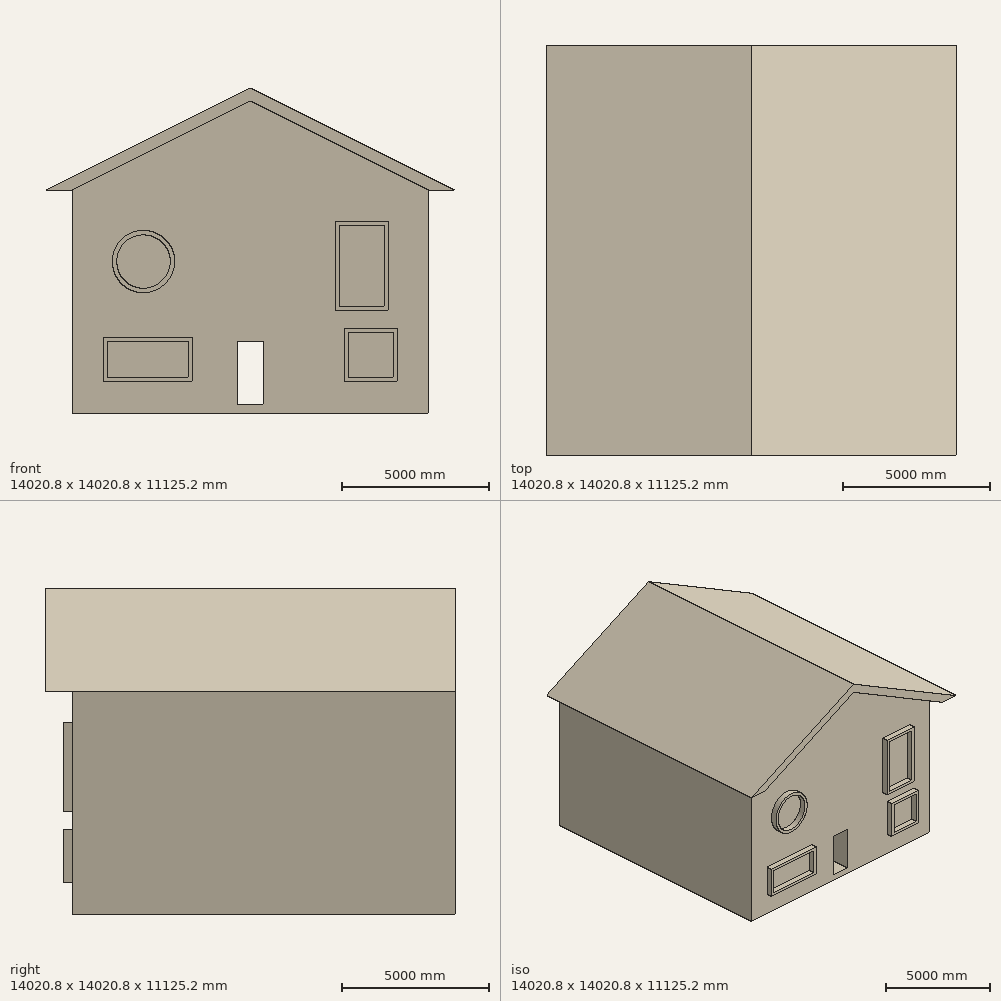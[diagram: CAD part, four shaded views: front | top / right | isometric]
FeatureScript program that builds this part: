
annotation { "Feature Type Name" : "Feature", "Feature Type Description" : "" }
export const myFeature = defineFeature(function(context is Context, id is Id, definition is map)
    precondition{}
    {
        {
            var Q0;
            Q0=qCreatedBy(makeId("Front.planeOp"),FACE);
            var sketch = newSketch(context, id + "F0", { "sketchPlane" : qUnion([Q0])});
            skLineSegment(sketch, "E0", {"start": v(0, 0) * mm, "end": v(-6096, 0) * mm});
            skLineSegment(sketch, "E1", {"start": v(0, 0) * mm, "end": v(6096, 0) * mm});
            skLineSegment(sketch, "E2", {"start": v(0, 0) * mm, "end": v(0, 3048) * mm, "construction": true});
            skLineSegment(sketch, "E3", {"start": v(-6096, 0) * mm, "end": v(0, 3048) * mm});
            skLineSegment(sketch, "E4", {"start": v(0, 3048) * mm, "end": v(6096, 0) * mm});
            skLineSegment(sketch, "E5", {"start": v(-6096, 0) * mm, "end": v(-7010.4, 0) * mm});
            skLineSegment(sketch, "E6", {"start": v(6096, 0) * mm, "end": v(7010.4, 0) * mm});
            skLineSegment(sketch, "E7", {"start": v(0, 3048) * mm, "end": v(0, 3505.2) * mm});
            skLineSegment(sketch, "E8", {"start": v(-7010.4, 0) * mm, "end": v(0, 3505.2) * mm});
            skLineSegment(sketch, "E9", {"start": v(0, 3505.2) * mm, "end": v(7010.4, 0) * mm});
            skLineSegment(sketch, "E10", {"start": v(-6096, 0) * mm, "end": v(-6096, -7315.2) * mm});
            skLineSegment(sketch, "E11", {"start": v(-6096, -7315.2) * mm, "end": v(6096, -7315.2) * mm});
            skLineSegment(sketch, "E12", {"start": v(6096, -7315.2) * mm, "end": v(6096, 0) * mm});
            skLineSegment(sketch, "E13", {"start": v(-6096, -7315.2) * mm, "end": v(-6096, -6423.42) * mm});
            skLineSegment(sketch, "E14", {"start": v(-6096, -7315.2) * mm, "end": v(-6096, -7620) * mm});
            skLineSegment(sketch, "E15", {"start": v(-6096, -7620) * mm, "end": v(6096, -7620) * mm});
            skLineSegment(sketch, "E16", {"start": v(6096, -7315.2) * mm, "end": v(6096, -7620) * mm});
            skLineSegment(sketch, "E17", {"start": v(0, -7315.2) * mm, "end": v(-457.2, -7315.2) * mm});
            skLineSegment(sketch, "E18", {"start": v(-457.2, -7315.2) * mm, "end": v(-457.2, -5181.6) * mm});
            skLineSegment(sketch, "E19", {"start": v(-457.2, -5181.6) * mm, "end": v(457.2, -5181.6) * mm});
            skLineSegment(sketch, "E20", {"start": v(457.2, -5181.6) * mm, "end": v(457.2, -7315.2) * mm});
            skLineSegment(sketch, "E21", {"start": v(0, -7315.2) * mm, "end": v(457.2, -7315.2) * mm});
            skLineSegment(sketch, "E22.bottom", {"start": v(-2133.6, -5181.6) * mm, "end": v(-4876.8, -5181.6) * mm});
            skLineSegment(sketch, "E22.top", {"start": v(-2133.6, -6400.8) * mm, "end": v(-4876.8, -6400.8) * mm});
            skLineSegment(sketch, "E22.left", {"start": v(-2133.6, -5181.6) * mm, "end": v(-2133.6, -6400.8) * mm});
            skLineSegment(sketch, "E22.right", {"start": v(-4876.8, -5181.6) * mm, "end": v(-4876.8, -6400.8) * mm});
            skLineSegment(sketch, "E23.0", {"start": v(-1981.2, -5029.2) * mm, "end": v(-1981.2, -6553.2) * mm});
            skLineSegment(sketch, "E23.1", {"start": v(-1981.2, -5029.2) * mm, "end": v(-5029.2, -5029.2) * mm});
            skLineSegment(sketch, "E23.2", {"start": v(-5029.2, -5029.2) * mm, "end": v(-5029.2, -6553.2) * mm});
            skLineSegment(sketch, "E23.3", {"start": v(-1981.2, -6553.2) * mm, "end": v(-5029.2, -6553.2) * mm});
            skLineSegment(sketch, "E24.bottom", {"start": v(3352.8, -4876.8) * mm, "end": v(4876.8, -4876.8) * mm});
            skLineSegment(sketch, "E24.top", {"start": v(3352.8, -6400.8) * mm, "end": v(4876.8, -6400.8) * mm});
            skLineSegment(sketch, "E24.left", {"start": v(3352.8, -4876.8) * mm, "end": v(3352.8, -6400.8) * mm});
            skLineSegment(sketch, "E24.right", {"start": v(4876.8, -4876.8) * mm, "end": v(4876.8, -6400.8) * mm});
            skLineSegment(sketch, "E25.0", {"start": v(5029.2, -4724.4) * mm, "end": v(5029.2, -6553.2) * mm});
            skLineSegment(sketch, "E25.1", {"start": v(3200.4, -4724.4) * mm, "end": v(5029.2, -4724.4) * mm});
            skLineSegment(sketch, "E25.2", {"start": v(3200.4, -4724.4) * mm, "end": v(3200.4, -6553.2) * mm});
            skLineSegment(sketch, "E25.3", {"start": v(3200.4, -6553.2) * mm, "end": v(5029.2, -6553.2) * mm});
            skCircle(sketch, "E26", {"center": v(-3657.6, -2438.4) * mm, "radius": 914.4 * mm});
            skCircle(sketch, "E27.0", {"center": v(-3657.6, -2438.4) * mm, "radius": 1066.8 * mm});
            skLineSegment(sketch, "E28.bottom", {"start": v(3048, -1219.2) * mm, "end": v(4572, -1219.2) * mm});
            skLineSegment(sketch, "E28.top", {"start": v(3048, -3962.4) * mm, "end": v(4572, -3962.4) * mm});
            skLineSegment(sketch, "E28.left", {"start": v(3048, -1219.2) * mm, "end": v(3048, -3962.4) * mm});
            skLineSegment(sketch, "E28.right", {"start": v(4572, -1219.2) * mm, "end": v(4572, -3962.4) * mm});
            skLineSegment(sketch, "E29.0", {"start": v(4724.4, -1066.8) * mm, "end": v(4724.4, -4114.8) * mm});
            skLineSegment(sketch, "E29.1", {"start": v(2895.6, -1066.8) * mm, "end": v(4724.4, -1066.8) * mm});
            skLineSegment(sketch, "E29.2", {"start": v(2895.6, -1066.8) * mm, "end": v(2895.6, -4114.8) * mm});
            skLineSegment(sketch, "E29.3", {"start": v(2895.6, -4114.8) * mm, "end": v(4724.4, -4114.8) * mm});
            skLineSegment(sketch, "E30.0", {"start": v(609.6, -5029.2) * mm, "end": v(609.6, -7315.2) * mm});
            skLineSegment(sketch, "E30.1", {"start": v(-609.6, -5029.2) * mm, "end": v(609.6, -5029.2) * mm});
            skLineSegment(sketch, "E30.2", {"start": v(-609.6, -7315.2) * mm, "end": v(-609.6, -5029.2) * mm});
            skSolve(sketch);
        }
        {
            var Q0;
            Q0=makeQuery(id+"F0.imprint","IMPRINT",FACE,{"disambiguationData":[TD([[makeQuery(id+"F0.imprint","IMPRINT",EDGE,{"derivedFrom":sQuery(id+"F0.wireOp",EDGE,"E3")}),1.0]])]});
            var Q1;
            Q1=makeQuery(id+"F0.imprint","IMPRINT",FACE,{"disambiguationData":[TD([[makeQuery(id+"F0.imprint","IMPRINT",EDGE,{"derivedFrom":sQuery(id+"F0.wireOp",EDGE,"E4")}),1.0]])]});
            extrude(context, id + "F1", {"entities" : qUnion([Q0, Q1]), "depth" : 14020.8 * mm, "offsetDistance" : 30.48 * mm});
        }
        {
            var Q0;
            Q0=makeQuery(id+"F0.imprint","IMPRINT",FACE,{"disambiguationData":[TD([[makeQuery(id+"F0.imprint","IMPRINT",EDGE,{"derivedFrom":sQuery(id+"F0.wireOp",EDGE,"E0")}),-1.0]])]});
            extrude(context, id + "F2", {"entities" : qUnion([Q0]), "operationType" : NewBodyOperationType.ADD, "depth" : 13106.4 * mm, "offsetDistance" : 30.48 * mm});
        }
        {
            var Q0;
            Q0=makeQuery(id+"F0.imprint","IMPRINT",FACE,{"disambiguationData":[TD([[makeQuery(id+"F0.imprint","IMPRINT",EDGE,{"derivedFrom":sQuery(id+"F0.wireOp",EDGE,"E4")}),1.0]])]});
            var Q1;
            Q1=makeQuery(id+"F0.imprint","IMPRINT",FACE,{"disambiguationData":[TD([[makeQuery(id+"F0.imprint","IMPRINT",EDGE,{"derivedFrom":sQuery(id+"F0.wireOp",EDGE,"E3")}),1.0]])]});
            extrude(context, id + "F3", {"entities" : qUnion([Q0, Q1]), "operationType" : NewBodyOperationType.ADD, "depth" : 914.4 * mm, "offsetDistance" : 30.48 * mm});
        }
        {
            var Q0;
            Q0=makeQuery(id+"F0.imprint","IMPRINT",FACE,{"disambiguationData":[TD([[makeQuery(id+"F0.imprint","IMPRINT",EDGE,{"derivedFrom":sQuery(id+"F0.wireOp",EDGE,"E0")}),1.0]])]});
            extrude(context, id + "F4", {"entities" : qUnion([Q0]), "operationType" : NewBodyOperationType.ADD, "depth" : 13106.4 * mm, "offsetDistance" : 30.48 * mm});
        }
        {
            var Q0;
            {var subQ0=sQuery(id+"F0.wireOp",EDGE,"E14");Q0=makeQuery(id+"F0.imprint","IMPRINT",FACE,{"disambiguationData":[TD([[makeQuery(id+"F0.imprint","IMPRINT",EDGE,{"derivedFrom":subQ0}),1.0]])]});}
            extrude(context, id + "F5", {"entities" : qUnion([Q0]), "operationType" : NewBodyOperationType.ADD, "depth" : 13106.4 * mm, "offsetDistance" : 30.48 * mm});
        }
        {
            var Q0;
            Q0=makeQuery(id+"F0.imprint","IMPRINT",FACE,{"disambiguationData":[TD([[makeQuery(id+"F0.imprint","IMPRINT",EDGE,{"derivedFrom":sQuery(id+"F0.wireOp",EDGE,"E28.bottom")}),-1.0]])]});
            var Q1;
            Q1=makeQuery(id+"F0.imprint","IMPRINT",FACE,{"disambiguationData":[TD([[makeQuery(id+"F0.imprint","IMPRINT",EDGE,{"derivedFrom":sQuery(id+"F0.wireOp",EDGE,"E24.bottom")}),-1.0]])]});
            var Q2;
            Q2=makeQuery(id+"F0.imprint","IMPRINT",FACE,{"disambiguationData":[TD([[makeQuery(id+"F0.imprint","IMPRINT",EDGE,{"derivedFrom":sQuery(id+"F0.wireOp",EDGE,"E22.bottom")}),1.0]])]});
            var Q3;
            Q3=makeQuery(id+"F0.imprint","IMPRINT",FACE,{"disambiguationData":[TD([[makeQuery(id+"F0.imprint","IMPRINT",EDGE,{"derivedFrom":sQuery(id+"F0.wireOp",EDGE,"E26")}),1.0]])]});
            extrude(context, id + "F6", {"entities" : qUnion([Q0, Q1, Q2, Q3]), "depth" : 13106.4 * mm, "offsetDistance" : 30.48 * mm});
        }
        {
            var Q0;
            Q0=makeQuery(id+"F0.imprint","IMPRINT",FACE,{"disambiguationData":[TD([[makeQuery(id+"F0.imprint","IMPRINT",EDGE,{"derivedFrom":sQuery(id+"F0.wireOp",EDGE,"E26")}),-1.0]])]});
            var Q1;
            Q1=makeQuery(id+"F0.imprint","IMPRINT",FACE,{"disambiguationData":[TD([[makeQuery(id+"F0.imprint","IMPRINT",EDGE,{"derivedFrom":sQuery(id+"F0.wireOp",EDGE,"E28.bottom")}),1.0]])]});
            var Q2;
            Q2=makeQuery(id+"F0.imprint","IMPRINT",FACE,{"disambiguationData":[TD([[makeQuery(id+"F0.imprint","IMPRINT",EDGE,{"derivedFrom":sQuery(id+"F0.wireOp",EDGE,"E22.bottom")}),-1.0]])]});
            var Q3;
            Q3=makeQuery(id+"F0.imprint","IMPRINT",FACE,{"disambiguationData":[TD([[makeQuery(id+"F0.imprint","IMPRINT",EDGE,{"derivedFrom":sQuery(id+"F0.wireOp",EDGE,"E24.bottom")}),1.0]])]});
            extrude(context, id + "F7", {"entities" : qUnion([Q0, Q1, Q2, Q3]), "depth" : 13411.2 * mm, "offsetDistance" : 30.48 * mm});
        }
        {
            var Q0;
            {var subQ0=sQuery(id+"F0.wireOp",EDGE,"E18");Q0=makeQuery(id+"F0.imprint","IMPRINT",FACE,{"disambiguationData":[TD([[makeQuery(id+"F0.imprint","IMPRINT",EDGE,{"derivedFrom":subQ0}),1.0]])]});}
            extrude(context, id + "F8", {"entities" : qUnion([Q0]), "operationType" : NewBodyOperationType.ADD, "depth" : 13106.4 * mm, "offsetDistance" : 30.48 * mm});
        }
    });
